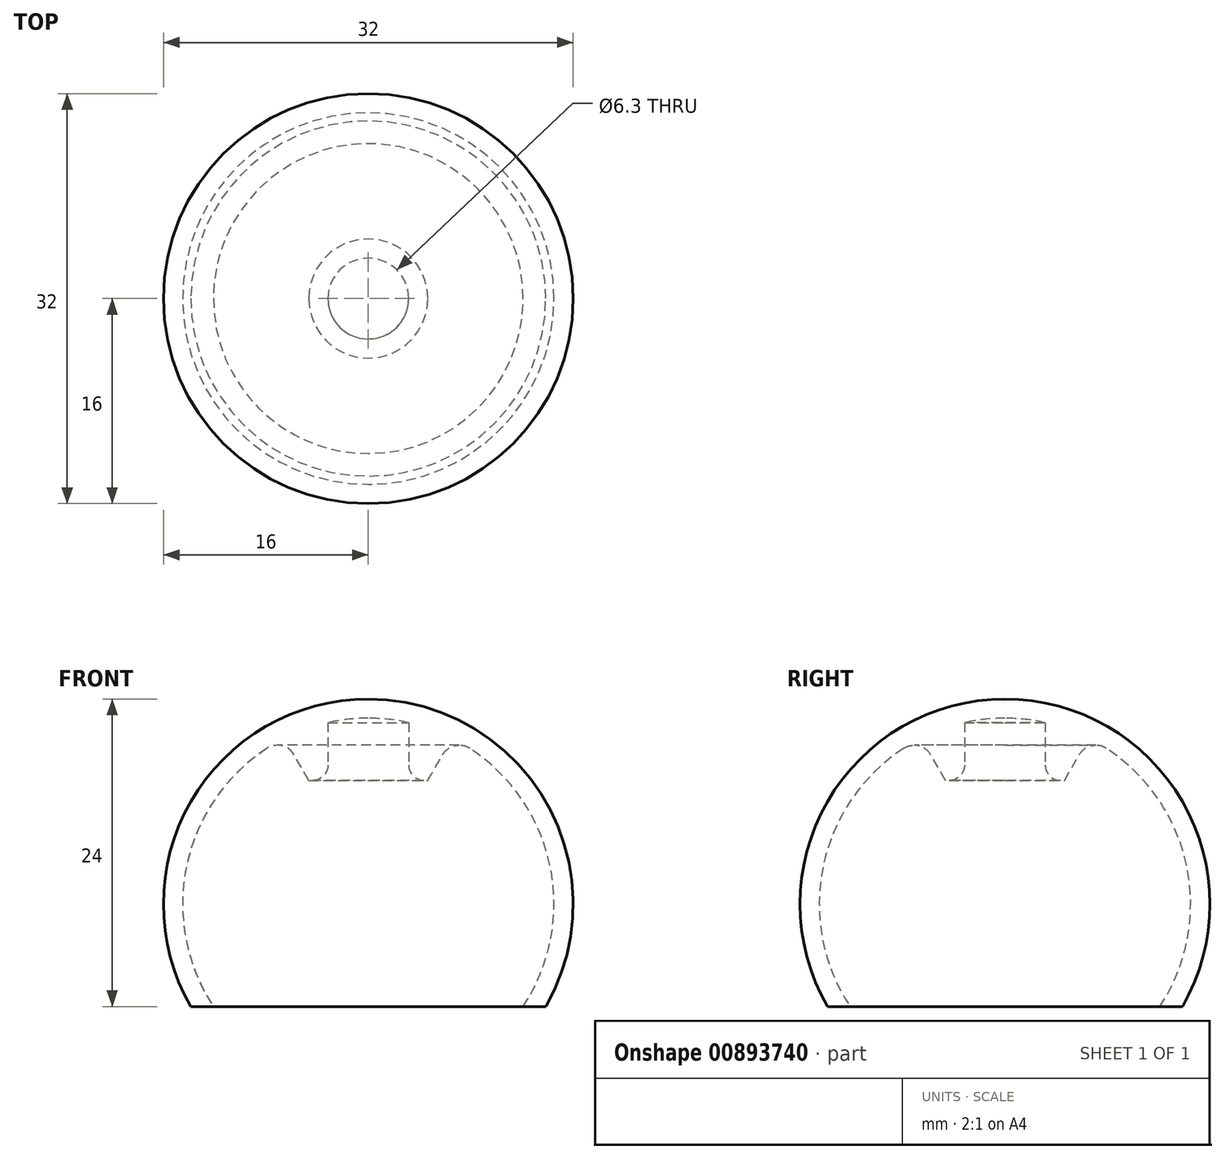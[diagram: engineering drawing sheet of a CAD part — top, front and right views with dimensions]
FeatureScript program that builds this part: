
annotation { "Feature Type Name" : "Feature", "Feature Type Description" : "" }
export const myFeature = defineFeature(function(context is Context, id is Id, definition is map)
    precondition{}
    {
        {
            var Q0;
            Q0=qCreatedBy(makeId("Front.planeOp"),FACE);
            var sketch = newSketch(context, id + "F0", { "sketchPlane" : qUnion([Q0])});
            skArc(sketch, "E0", {"start": v(0, 24) * mm, "mid": v(-13.86, 16) * mm, "end": v(-13.86, 0) * mm});
            skPoint(sketch, "E1", {"position": v(0, 24) * mm});
            skArc(sketch, "E2.0", {"start": v(0, 22.5) * mm, "mid": v(-12.77, 14.86) * mm, "end": v(-12.1, 0) * mm});
            skLineSegment(sketch, "E3", {"start": v(-13.86, 0) * mm, "end": v(-12.1, 0) * mm});
            skPoint(sketch, "E4.orphan", {"position": v(12.1, 0) * mm});
            skPoint(sketch, "E5.orphan", {"position": v(13.86, 0) * mm});
            skLineSegment(sketch, "E6", {"start": v(-4.65, 21.73) * mm, "end": v(-4.65, 17.65) * mm});
            skLineSegment(sketch, "E7", {"start": v(-4.65, 17.65) * mm, "end": v(-3.15, 17.65) * mm});
            skLineSegment(sketch, "E8", {"start": v(-3.15, 17.65) * mm, "end": v(-3.15, 22.15) * mm});
            skLineSegment(sketch, "E9", {"start": v(0, 22.5) * mm, "end": v(0, 24) * mm});
            skLineSegment(sketch, "E10", {"start": v(-4.65, 17.65) * mm, "end": v(-6.55, 20.94) * mm});
            skLineSegment(sketch, "E11", {"start": v(-12.1, 0) * mm, "end": v(19.96, 21.2) * mm, "construction": true});
            skSolve(sketch);
        }
        {
            var Q0;
            Q0=qSketchRegion(id+"F0",true);
            var Q1;
            Q1=sQuery(id+"F0.wireOp",EDGE,"E9");
            revolve(context, id + "F1", {"surfaceOperationType" : NewSurfaceOperationType.NEW, "entities" : qUnion([Q0]), "axis" : qUnion([Q1]), "revolveType" : RevolveType.FULL});
        }
        {
            var Q0;
            Q0=makeQuery(id+"F1.opRevolve","SWEPT_EDGE",EDGE,{"disambiguationData":[OSD([sQuery(id+"F0.wireOp",EDGE,"E7"),sQuery(id+"F0.wireOp",EDGE,"E8")])]});
            fillet(context, id + "F2", {"entities" : qUnion([Q0]), "radius" : 1.2 * mm, "tangentPropagation" : true, "allowEdgeOverflow" : false});
        }
        {
            var Q0;
            Q0=makeQuery(id+"F1.opRevolve","SWEPT_EDGE",EDGE,{"disambiguationData":[OSD([sQuery(id+"F0.wireOp",EDGE,"E2.0"),sQuery(id+"F0.wireOp",EDGE,"E10")])]});
            fillet(context, id + "F3", {"entities" : qUnion([Q0]), "radius" : 1.5 * mm, "tangentPropagation" : true, "allowEdgeOverflow" : false});
        }
    });
